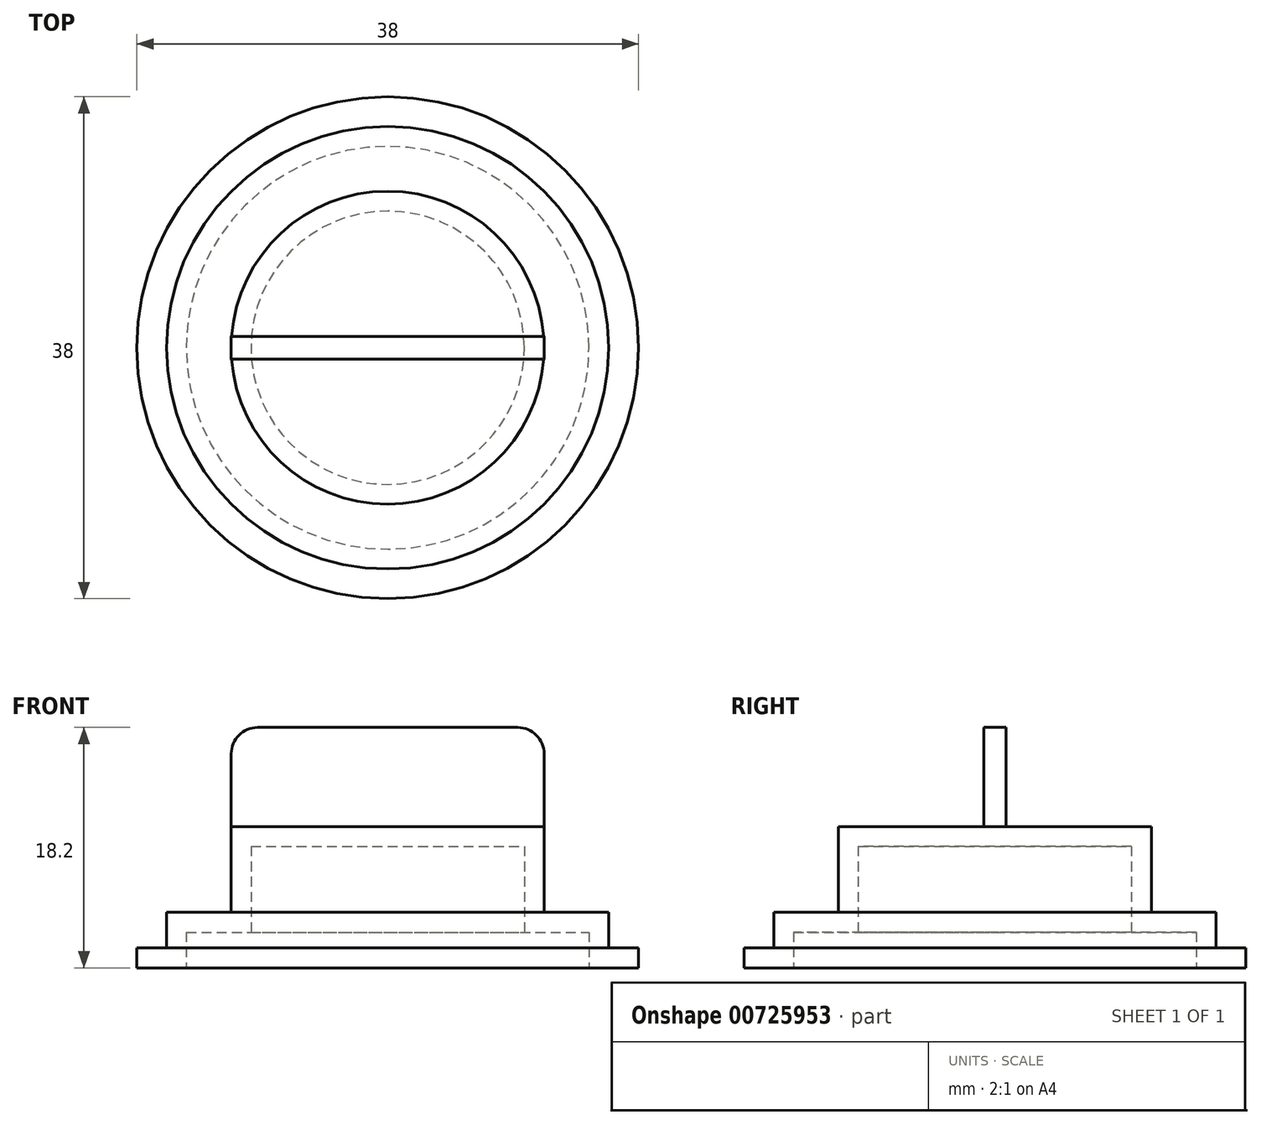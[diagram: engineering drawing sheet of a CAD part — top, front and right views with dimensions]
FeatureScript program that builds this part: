
annotation { "Feature Type Name" : "Feature", "Feature Type Description" : "" }
export const myFeature = defineFeature(function(context is Context, id is Id, definition is map)
    precondition{}
    {
        {
            var Q0;
            Q0=qCreatedBy(makeId("Front.planeOp"),FACE);
            var sketch = newSketch(context, id + "F0", { "sketchPlane" : qUnion([Q0])});
            skLineSegment(sketch, "E0", {"start": v(0, 0) * mm, "end": v(-11.85, 0) * mm});
            skLineSegment(sketch, "E1", {"start": v(-11.85, 0) * mm, "end": v(-11.85, -6.5) * mm});
            skLineSegment(sketch, "E2", {"start": v(-11.85, -6.5) * mm, "end": v(-16.75, -6.5) * mm});
            skLineSegment(sketch, "E3", {"start": v(-16.75, -6.5) * mm, "end": v(-16.75, -9.2) * mm});
            skLineSegment(sketch, "E4", {"start": v(-16.75, -9.2) * mm, "end": v(-19, -9.2) * mm});
            skLineSegment(sketch, "E5", {"start": v(-19, -9.2) * mm, "end": v(-19, -10.7) * mm});
            skLineSegment(sketch, "E6", {"start": v(-19, -10.7) * mm, "end": v(-15.25, -10.7) * mm});
            skLineSegment(sketch, "E7", {"start": v(-15.25, -10.7) * mm, "end": v(-15.25, -8) * mm});
            skLineSegment(sketch, "E8", {"start": v(-15.25, -8) * mm, "end": v(-10.35, -8) * mm});
            skLineSegment(sketch, "E9", {"start": v(-10.35, -8) * mm, "end": v(-10.35, -1.5) * mm});
            skLineSegment(sketch, "E10", {"start": v(-10.35, -1.5) * mm, "end": v(0, -1.5) * mm});
            skLineSegment(sketch, "E11", {"start": v(0, -1.5) * mm, "end": v(0, 0) * mm});
            skSolve(sketch);
        }
        {
            var Q0;
            Q0=makeQuery(id+"F0.imprint","IMPRINT",FACE,{"disambiguationData":[TD([[makeQuery(id+"F0.imprint","IMPRINT",EDGE,{"derivedFrom":sQuery(id+"F0.wireOp",EDGE,"E0")}),1.0]])]});
            var Q1;
            Q1=sQuery(id+"F0.wireOp",EDGE,"E11");
            revolve(context, id + "F1", {"surfaceOperationType" : NewSurfaceOperationType.NEW, "entities" : qUnion([Q0]), "axis" : qUnion([Q1]), "revolveType" : RevolveType.FULL});
        }
        {
            var Q0;
            Q0=qCreatedBy(makeId("Top.planeOp"),FACE);
            var sketch = newSketch(context, id + "F2", { "sketchPlane" : qUnion([Q0])});
            skLineSegment(sketch, "E12.bottom", {"start": v(-11.85, 0.85) * mm, "end": v(11.85, 0.85) * mm});
            skLineSegment(sketch, "E12.top", {"start": v(-11.85, -0.85) * mm, "end": v(11.85, -0.85) * mm});
            skLineSegment(sketch, "E12.left", {"start": v(-11.85, 0.85) * mm, "end": v(-11.85, -0.85) * mm});
            skLineSegment(sketch, "E12.right", {"start": v(11.85, 0.85) * mm, "end": v(11.85, -0.85) * mm});
            skPoint(sketch, "E12.middle", {"position": v(0, 0) * mm});
            skSolve(sketch);
        }
        {
            var Q0;
            Q0 = qSketchRegion(id + "F2", true);
            extrude(context, id + "F3", {"entities" : qUnion([Q0]), "operationType" : NewBodyOperationType.ADD, "depth" : 7.5 * mm, "offsetDistance" : 25 * mm});
        }
        {
            var Q0;
            Q0=makeQuery(id+"F3.opExtrude","CAP_EDGE",EDGE,{"disambiguationData":[OSD([sQuery(id+"F2.wireOp",EDGE,"E12.left")])],"isStart":false});
            fillet(context, id + "F4", {"entities" : qUnion([Q0]), "radius" : 2 * mm, "tangentPropagation" : true, "allowEdgeOverflow" : false});
        }
        {
            var Q0;
            Q0=makeQuery(id+"F3.opExtrude","CAP_EDGE",EDGE,{"disambiguationData":[OSD([sQuery(id+"F2.wireOp",EDGE,"E12.right")])],"isStart":false});
            fillet(context, id + "F5", {"entities" : qUnion([Q0]), "radius" : 2 * mm, "tangentPropagation" : true, "allowEdgeOverflow" : false});
        }
    });
